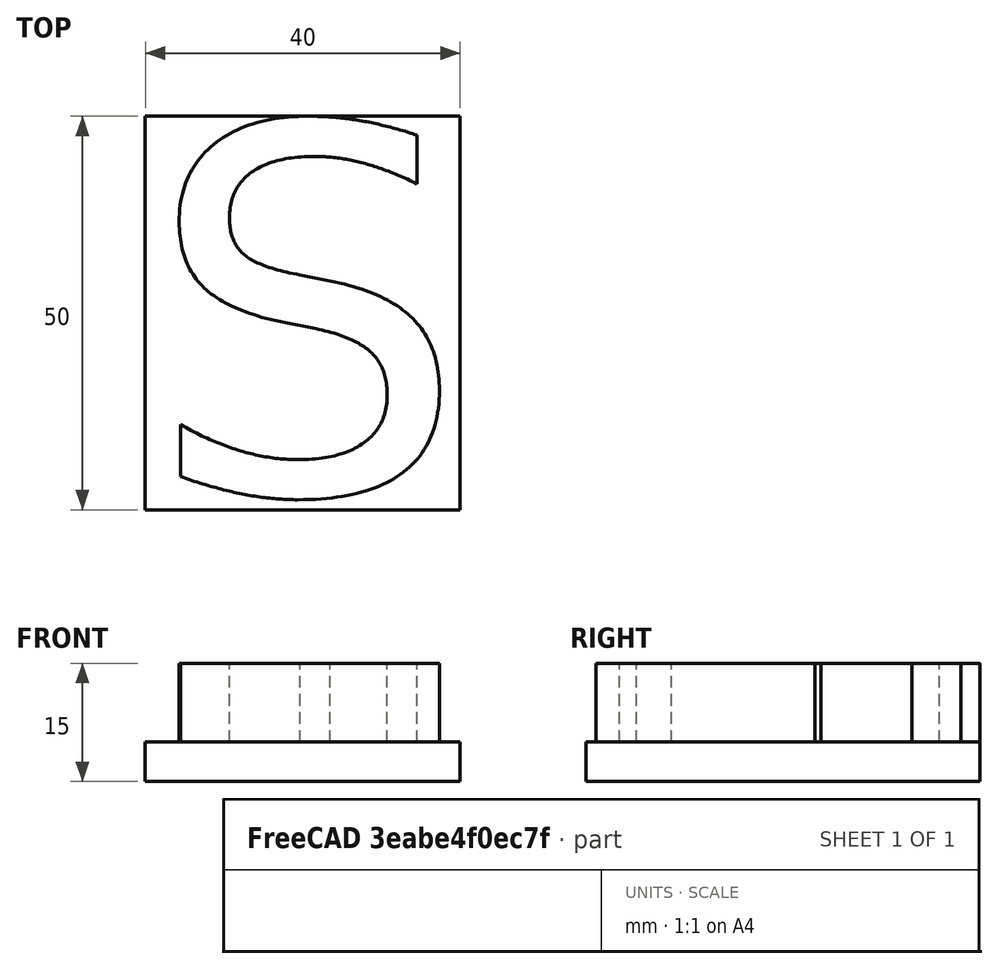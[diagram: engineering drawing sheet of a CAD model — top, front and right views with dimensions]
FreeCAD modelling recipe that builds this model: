
FCSTD DOCUMENT  (FreeCAD 0.21RUnknown)
Label: s
License: All rights reserved
LicenseURL: https://en.wikipedia.org/wiki/All_rights_reserved
objects: Part::Part2DObjectPython×2, Part::Extrusion×2
note: 4 computed .brp shape members not serialized (recipe doc carries the construction recipe); baked Part::Feature solids carry a one-line shape summary decoded from their .brp

FEATURE [Part::Part2DObjectPython] Rectangle  # Draft 2D object (typed FeaturePython)
  Area = 2000
  ChamferSize = 0
  Columns = 1
  FilletRadius = 0
  Height = 50
  Length = 40
  MakeFace = true
  Placement = pos=(-0.0534207,-0.213677,0) rot=(0,0,1;0rad)
  Rows = 1
FEATURE [Part::Extrusion] Extrusion
  Base = -> Rectangle
  Dir = (0,0,5)
  DirMode = 0
  FaceMakerClass = Part::FaceMakerBullseye
  LengthFwd = 0
  LengthRev = 0
  Solid = true
  Symmetric = false
FEATURE [Part::Part2DObjectPython] ShapeString  # Draft 2D object (typed FeaturePython)
  FontFile = /nix/var/nix/profiles/system/sw/share/X11/fonts/DejaVuSans.ttf
  MakeFace = true
  Placement = pos=(0,2,5) rot=(0,0,1;0rad)
  Size = 50
  String = S
  Tracking = 0
FEATURE [Part::Extrusion] Extrude
  Base = -> ShapeString
  Dir = (0,0,1)
  DirMode = 2
  FaceMakerClass = Part::FaceMakerBullseye
  LengthFwd = 10
  LengthRev = 0
  Solid = true
  Symmetric = false
  TaperAngleRev = 0.01
